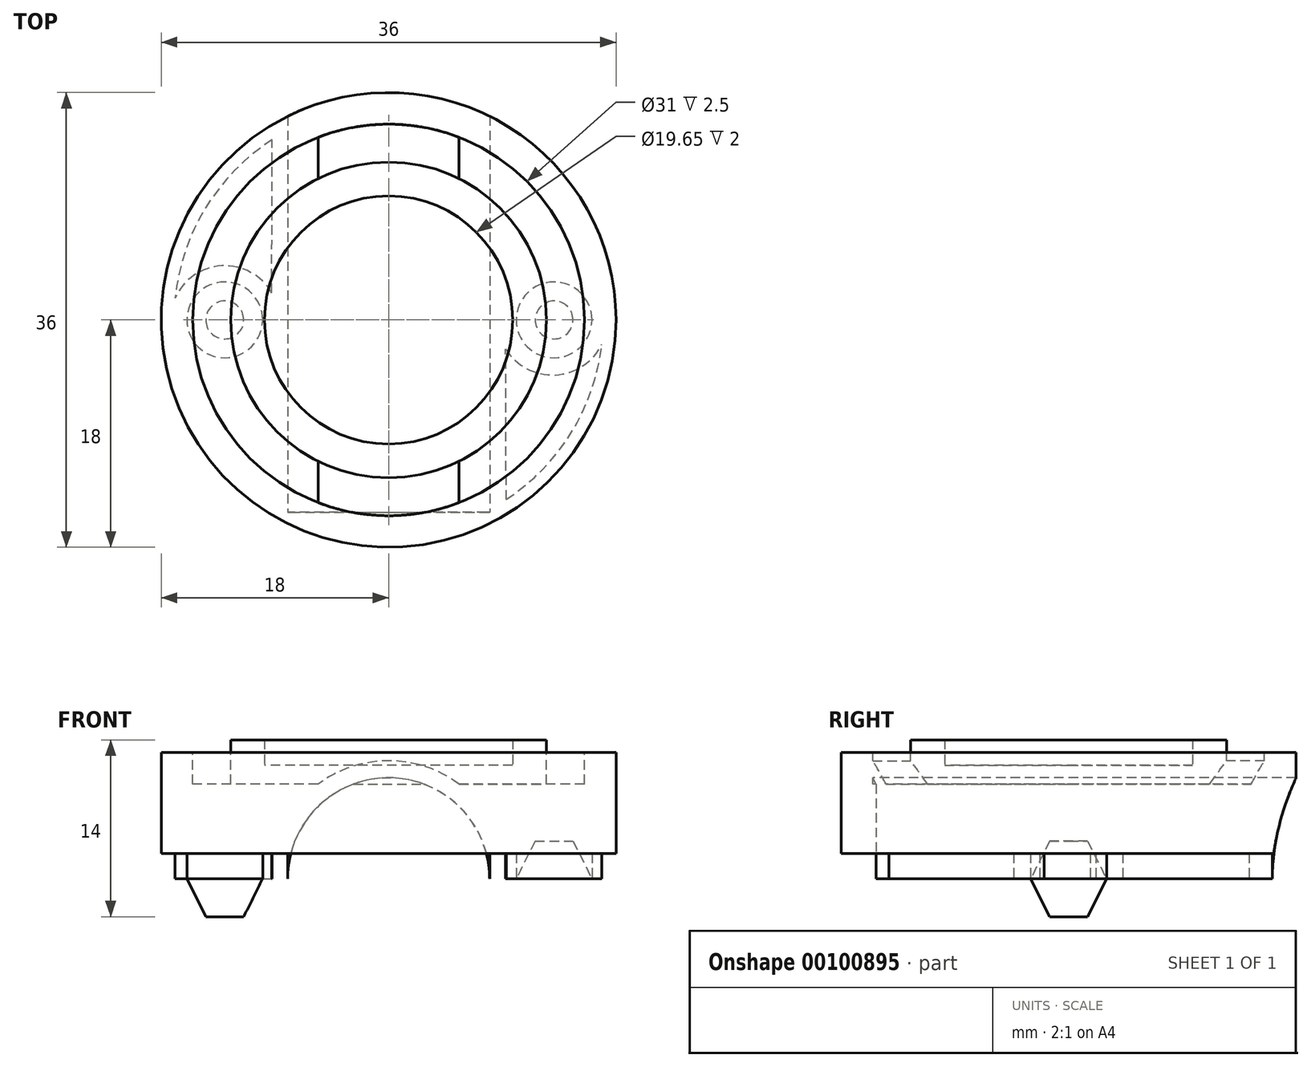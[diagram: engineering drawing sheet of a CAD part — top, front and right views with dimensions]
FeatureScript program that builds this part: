
annotation { "Feature Type Name" : "Feature", "Feature Type Description" : "" }
export const myFeature = defineFeature(function(context is Context, id is Id, definition is map)
    precondition{}
    {
        {
            var Q0;
            Q0=qCreatedBy(makeId("Top.planeOp"),FACE);
            var sketch = newSketch(context, id + "F0", { "sketchPlane" : qUnion([Q0])});
            skCircle(sketch, "E0", {"center": v(0, 0) * mm, "radius": 18 * mm});
            skSolve(sketch);
        }
        {
            var Q0;
            Q0 = qSketchRegion(id + "F0", true);
            extrude(context, id + "F1", {"entities" : qUnion([Q0]), "depth" : 10 * mm});
        }
        {
            var Q0;
            Q0=makeQuery(id+"F1.opExtrude","CAP_FACE",FACE,{"disambiguationData":[OSD([sQuery(id+"F0.wireOp",EDGE,"E0")])],"isStart":false});
            var sketch = newSketch(context, id + "F2", { "sketchPlane" : qUnion([Q0])});
            skCircle(sketch, "E1", {"center": v(0, 0) * mm, "radius": 15.5 * mm});
            skCircle(sketch, "E2", {"center": v(0, 0) * mm, "radius": 12.5 * mm});
            skSolve(sketch);
        }
        {
            var Q0;
            Q0=makeQuery(id+"F2.imprint","IMPRINT",FACE,{"disambiguationData":[TD([[makeQuery(id+"F2.imprint","IMPRINT",EDGE,{"derivedFrom":sQuery(id+"F2.wireOp",EDGE,"E1")}),1.0]])]});
            extrude(context, id + "F3", {"entities" : qUnion([Q0]), "operationType" : NewBodyOperationType.REMOVE, "oppositeDirection" : true, "depth" : 2.5 * mm});
        }
        {
            var Q0;
            Q0=makeQuery(id+"F3.boolean.opBoolean","SPLIT",FACE,{"disambiguationData":[TD([makeQuery(id+"F3.opExtrude","SWEPT_FACE",FACE,{"disambiguationData":[OSD([sQuery(id+"F2.wireOp",EDGE,"E2")])]})])],"derivedFrom":makeQuery(id+"F1.opExtrude","CAP_FACE",FACE,{"disambiguationData":[OSD([sQuery(id+"F0.wireOp",EDGE,"E0")])],"isStart":false})});
            var sketch = newSketch(context, id + "F4", { "sketchPlane" : qUnion([Q0])});
            skCircle(sketch, "E3", {"center": v(0, 0) * mm, "radius": 9.82 * mm});
            skSolve(sketch);
        }
        {
            var Q0;
            Q0=makeQuery(id+"F4.imprint","IMPRINT",FACE,{"disambiguationData":[TD([[makeQuery(id+"F4.imprint","IMPRINT",EDGE,{"derivedFrom":sQuery(id+"F4.wireOp",EDGE,"E3")}),-1.0]])]});
            extrude(context, id + "F5", {"entities" : qUnion([Q0]), "operationType" : NewBodyOperationType.ADD, "depth" : 1 * mm});
        }
        {
            var Q0;
            Q0=makeQuery(id+"F3.boolean.opBoolean","SPLIT",FACE,{"disambiguationData":[TD([makeQuery(id+"F3.opExtrude","SWEPT_FACE",FACE,{"disambiguationData":[OSD([sQuery(id+"F2.wireOp",EDGE,"E2")])]})])],"derivedFrom":makeQuery(id+"F1.opExtrude","CAP_FACE",FACE,{"disambiguationData":[OSD([sQuery(id+"F0.wireOp",EDGE,"E0")])],"isStart":false})});
            extrude(context, id + "F6", {"entities" : qUnion([Q0]), "operationType" : NewBodyOperationType.REMOVE, "oppositeDirection" : true, "depth" : 1 * mm});
        }
        {
            var Q0;
            Q0=qCreatedBy(makeId("Front.planeOp"),FACE);
            var sketch = newSketch(context, id + "F7", { "sketchPlane" : qUnion([Q0])});
            skPoint(sketch, "E4", {"position": v(0, 0) * mm});
            skArc(sketch, "E5", {"start": v(8, 0) * mm, "mid": v(0, 8) * mm, "end": v(-8, 0) * mm});
            skLineSegment(sketch, "E6", {"start": v(-8, 0) * mm, "end": v(8, 0) * mm});
            skSolve(sketch);
        }
        {
            var Q0;
            Q0=qCreatedBy(makeId("Front.planeOp"),FACE);
            var sketch = newSketch(context, id + "F8", { "sketchPlane" : qUnion([Q0])});
            skPoint(sketch, "E7", {"position": v(0, 0) * mm});
            skArc(sketch, "E8", {"start": v(4.95, 6.28) * mm, "mid": v(0, 8) * mm, "end": v(-4.95, 6.28) * mm});
            skLineSegment(sketch, "E9", {"start": v(-8, 0) * mm, "end": v(8, 0) * mm});
            skArc(sketch, "E10", {"start": v(6.92, 6.28) * mm, "mid": v(0, 9.35) * mm, "end": v(-6.92, 6.28) * mm});
            skLineSegment(sketch, "E11", {"start": v(6.92, 6.28) * mm, "end": v(4.95, 6.28) * mm});
            skLineSegment(sketch, "E12", {"start": v(-4.95, 6.28) * mm, "end": v(-6.92, 6.28) * mm});
            skSolve(sketch);
        }
        {
            var Q0;
            Q0 = qSketchRegion(id + "F7", true);
            extrude(context, id + "F9", {"entities" : qUnion([Q0]), "operationType" : NewBodyOperationType.REMOVE, "oppositeDirection" : true, "depth" : 19.92 * mm, "hasSecondDirection" : true, "secondDirectionOppositeDirection" : false, "secondDirectionDepth" : 15.24 * mm});
        }
        {
            var Q0;
            Q0=makeQuery(id+"F1.opExtrude","CAP_FACE",FACE,{"disambiguationData":[OSD([sQuery(id+"F0.wireOp",EDGE,"E0")])],"isStart":true});
            var sketch = newSketch(context, id + "F10", { "sketchPlane" : qUnion([Q0])});
            skCircle(sketch, "E13", {"center": v(13.1, 0) * mm, "radius": 3 * mm});
            skSolve(sketch);
        }
        {
            var Q0;
            Q0=makeQuery(id+"F10.imprint","IMPRINT",FACE,{"disambiguationData":[TD([[makeQuery(id+"F10.imprint","IMPRINT",EDGE,{"derivedFrom":sQuery(id+"F10.wireOp",EDGE,"E13")}),1.0]])]});
            extrude(context, id + "F11", {"entities" : qUnion([Q0]), "operationType" : NewBodyOperationType.REMOVE, "oppositeDirection" : true, "depth" : 3 * mm});
        }
        {
            var Q0;
            Q0=makeQuery(id+"F1.opExtrude","CAP_FACE",FACE,{"disambiguationData":[OSD([sQuery(id+"F0.wireOp",EDGE,"E0")])],"isStart":true});
            var sketch = newSketch(context, id + "F12", { "sketchPlane" : qUnion([Q0])});
            skCircle(sketch, "E14", {"center": v(-12.97, 0) * mm, "radius": 3 * mm});
            skSolve(sketch);
        }
        {
            var Q0;
            Q0 = qSketchRegion(id + "F12", true);
            extrude(context, id + "F13", {"entities" : qUnion([Q0]), "operationType" : NewBodyOperationType.ADD, "depth" : 3 * mm});
        }
        {
            var Q0;
            Q0=makeQuery(id+"F13.opExtrude","CAP_EDGE",EDGE,{"disambiguationData":[OSD([sQuery(id+"F12.wireOp",EDGE,"E14")])],"isStart":false});
            chamfer(context, id + "F14", {"entities" : qUnion([Q0]), "chamferType" : ChamferType.TWO_OFFSETS, "width1" : 1.5 * mm, "oppositeDirection" : false, "width2" : 3 * mm, "tangentPropagation" : true});
        }
        {
            var Q0;
            Q0=makeQuery(id+"F11.boolean.opBoolean","COPY",EDGE,{"derivedFrom":makeQuery(id+"F11.opExtrude","CAP_EDGE",EDGE,{"disambiguationData":[OSD([sQuery(id+"F10.wireOp",EDGE,"E13")])],"isStart":false})});
            chamfer(context, id + "F15", {"entities" : qUnion([Q0]), "chamferType" : ChamferType.TWO_OFFSETS, "width1" : 1.5 * mm, "oppositeDirection" : false, "width2" : 3 * mm, "tangentPropagation" : true});
        }
        {
            var Q0;
            Q0=makeQuery(id+"F1.opExtrude","CAP_FACE",FACE,{"disambiguationData":[OSD([sQuery(id+"F0.wireOp",EDGE,"E0")])],"isStart":true});
            var sketch = newSketch(context, id + "F16", { "sketchPlane" : qUnion([Q0])});
            skArc(sketch, "E15", {"start": v(-9.3, 14.21) * mm, "mid": v(-14.46, 8.91) * mm, "end": v(-16.88, 1.93) * mm});
            skLineSegment(sketch, "E16", {"start": v(-9.3, 14.21) * mm, "end": v(-9.27, 2.3) * mm});
            skArc(sketch, "E17", {"start": v(-9.27, 2.3) * mm, "mid": v(-13.18, 4.35) * mm, "end": v(-16.88, 1.93) * mm});
            skArc(sketch, "E18", {"start": v(-9.25, -2.14) * mm, "mid": v(-13.2, -4.29) * mm, "end": v(-16.9, -1.72) * mm});
            skArc(sketch, "E19.MirrorCS", {"start": v(9.3, 14.21) * mm, "mid": v(14.46, 8.91) * mm, "end": v(16.88, 1.93) * mm});
            skLineSegment(sketch, "E20.MirrorCS", {"start": v(9.3, 14.21) * mm, "end": v(9.27, 2.3) * mm});
            skArc(sketch, "E21.MirrorCS", {"start": v(9.27, 2.3) * mm, "mid": v(13.18, 4.35) * mm, "end": v(16.88, 1.93) * mm});
            skArc(sketch, "E22.MirrorCS", {"start": v(9.25, -2.14) * mm, "mid": v(13.2, -4.29) * mm, "end": v(16.9, -1.72) * mm});
            skLineSegment(sketch, "E23.trimOffspring", {"start": v(-9.25, -2.14) * mm, "end": v(-9.21, -14.28) * mm});
            skArc(sketch, "E24.trimOffspring", {"start": v(-16.9, -1.72) * mm, "mid": v(-14.49, -8.87) * mm, "end": v(-9.21, -14.28) * mm});
            skLineSegment(sketch, "E25.trimOffspring", {"start": v(9.25, -2.14) * mm, "end": v(9.21, -14.28) * mm});
            skArc(sketch, "E26.trimOffspring", {"start": v(16.9, -1.72) * mm, "mid": v(14.49, -8.87) * mm, "end": v(9.21, -14.28) * mm});
            skSolve(sketch);
        }
        {
            var Q0;
            Q0=makeQuery(id+"F16.imprint","IMPRINT",FACE,{"disambiguationData":[TD([[makeQuery(id+"F16.imprint","IMPRINT",EDGE,{"derivedFrom":sQuery(id+"F16.wireOp",EDGE,"E15")}),1.0]])]});
            var Q1;
            Q1=makeQuery(id+"F16.imprint","IMPRINT",FACE,{"disambiguationData":[TD([[makeQuery(id+"F16.imprint","IMPRINT",EDGE,{"derivedFrom":sQuery(id+"F16.wireOp",EDGE,"E18")}),1.0]])]});
            var Q2;
            Q2=makeQuery(id+"F16.imprint","IMPRINT",FACE,{"disambiguationData":[TD([[makeQuery(id+"F16.imprint","IMPRINT",EDGE,{"derivedFrom":sQuery(id+"F16.wireOp",EDGE,"E19.MirrorCS")}),-1.0]])]});
            var Q3;
            Q3=makeQuery(id+"F16.imprint","IMPRINT",FACE,{"disambiguationData":[TD([[makeQuery(id+"F16.imprint","IMPRINT",EDGE,{"derivedFrom":sQuery(id+"F16.wireOp",EDGE,"E22.MirrorCS")}),-1.0]])]});
            extrude(context, id + "F17", {"entities" : qUnion([Q0, Q1, Q2, Q3]), "operationType" : NewBodyOperationType.REMOVE, "oppositeDirection" : true, "depth" : 2 * mm});
        }
        {
            var Q0;
            Q0 = qSketchRegion(id + "F8", true);
            var Q1;
            Q1=makeQuery(id+"F3.boolean.opBoolean","COPY",FACE,{"derivedFrom":makeQuery(id+"F3.opExtrude","SWEPT_FACE",FACE,{"disambiguationData":[OSD([sQuery(id+"F2.wireOp",EDGE,"E1")])]})});
            var Q2;
            {var subQ0=sQuery(id+"F2.wireOp",EDGE,"E2");Q2=makeQuery(id+"F5.boolean.opBoolean","MERGE",FACE,{"derivedFrom":[makeQuery(id+"F3.boolean.opBoolean","COPY",FACE,{"derivedFrom":makeQuery(id+"F3.opExtrude","SWEPT_FACE",FACE,{"disambiguationData":[OSD([subQ0])]})}),makeQuery(id+"F5.opExtrude","SWEPT_FACE",FACE,{"disambiguationData":[OSD([subQ0])]})]});}
            extrude(context, id + "F18", {"entities" : qUnion([Q0]), "operationType" : NewBodyOperationType.ADD, "endBound" : BoundingType.UP_TO_SURFACE, "endBoundEntityFace" : qUnion([Q1]), "depth" : 25.4 * mm, "hasSecondDirection" : true, "secondDirectionBound" : SecondDirectionBoundingType.UP_TO_SURFACE, "secondDirectionOppositeDirection" : false, "secondDirectionBoundEntityFace" : qUnion([Q2]), "secondDirectionDepth" : 25.4 * mm});
        }
        {
            var Q0;
            Q0 = qSketchRegion(id + "F8", true);
            var Q1;
            {var subQ0=sQuery(id+"F2.wireOp",EDGE,"E1");Q1=makeQuery(id+"F18.boolean.opBoolean","SPLIT",FACE,{"disambiguationData":[TD([makeQuery(id+"F1.opExtrude","CAP_FACE",FACE,{"disambiguationData":[OSD([sQuery(id+"F0.wireOp",EDGE,"E0")])],"isStart":false}),makeQuery(id+"F3.boolean.opBoolean","COPY",FACE,{"derivedFrom":makeQuery(id+"F3.opExtrude","CAP_FACE",FACE,{"disambiguationData":[OSD([subQ0,sQuery(id+"F2.wireOp",EDGE,"E2")])],"isStart":false})}),makeQuery(id+"F9.boolean.opBoolean","COPY",FACE,{"derivedFrom":makeQuery(id+"F9.opExtrude","SWEPT_FACE",FACE,{"disambiguationData":[OSD([sQuery(id+"F7.wireOp",EDGE,"E5")])]})}),makeQuery(id+"F18.opExtrude","SWEPT_FACE",FACE,{"disambiguationData":[OSD([sQuery(id+"F8.wireOp",EDGE,"E8")])]}),makeQuery(id+"F18.opExtrude","SWEPT_FACE",FACE,{"disambiguationData":[OSD([sQuery(id+"F8.wireOp",EDGE,"E10")])]})])],"derivedFrom":makeQuery(id+"F3.boolean.opBoolean","COPY",FACE,{"derivedFrom":makeQuery(id+"F3.opExtrude","SWEPT_FACE",FACE,{"disambiguationData":[OSD([subQ0])]})})});}
            var Q2;
            {var subQ0=sQuery(id+"F2.wireOp",EDGE,"E2");Q2=makeQuery(id+"F5.boolean.opBoolean","MERGE",FACE,{"derivedFrom":[makeQuery(id+"F3.boolean.opBoolean","COPY",FACE,{"derivedFrom":makeQuery(id+"F3.opExtrude","SWEPT_FACE",FACE,{"disambiguationData":[OSD([subQ0])]})}),makeQuery(id+"F5.opExtrude","SWEPT_FACE",FACE,{"disambiguationData":[OSD([subQ0])]})]});}
            extrude(context, id + "F19", {"entities" : qUnion([Q0]), "operationType" : NewBodyOperationType.ADD, "endBound" : BoundingType.UP_TO_SURFACE, "oppositeDirection" : true, "endBoundEntityFace" : qUnion([Q1]), "depth" : 25.4 * mm, "hasSecondDirection" : true, "secondDirectionBound" : SecondDirectionBoundingType.UP_TO_SURFACE, "secondDirectionOppositeDirection" : true, "secondDirectionBoundEntityFace" : qUnion([Q2]), "secondDirectionDepth" : 25.4 * mm});
        }
    });
